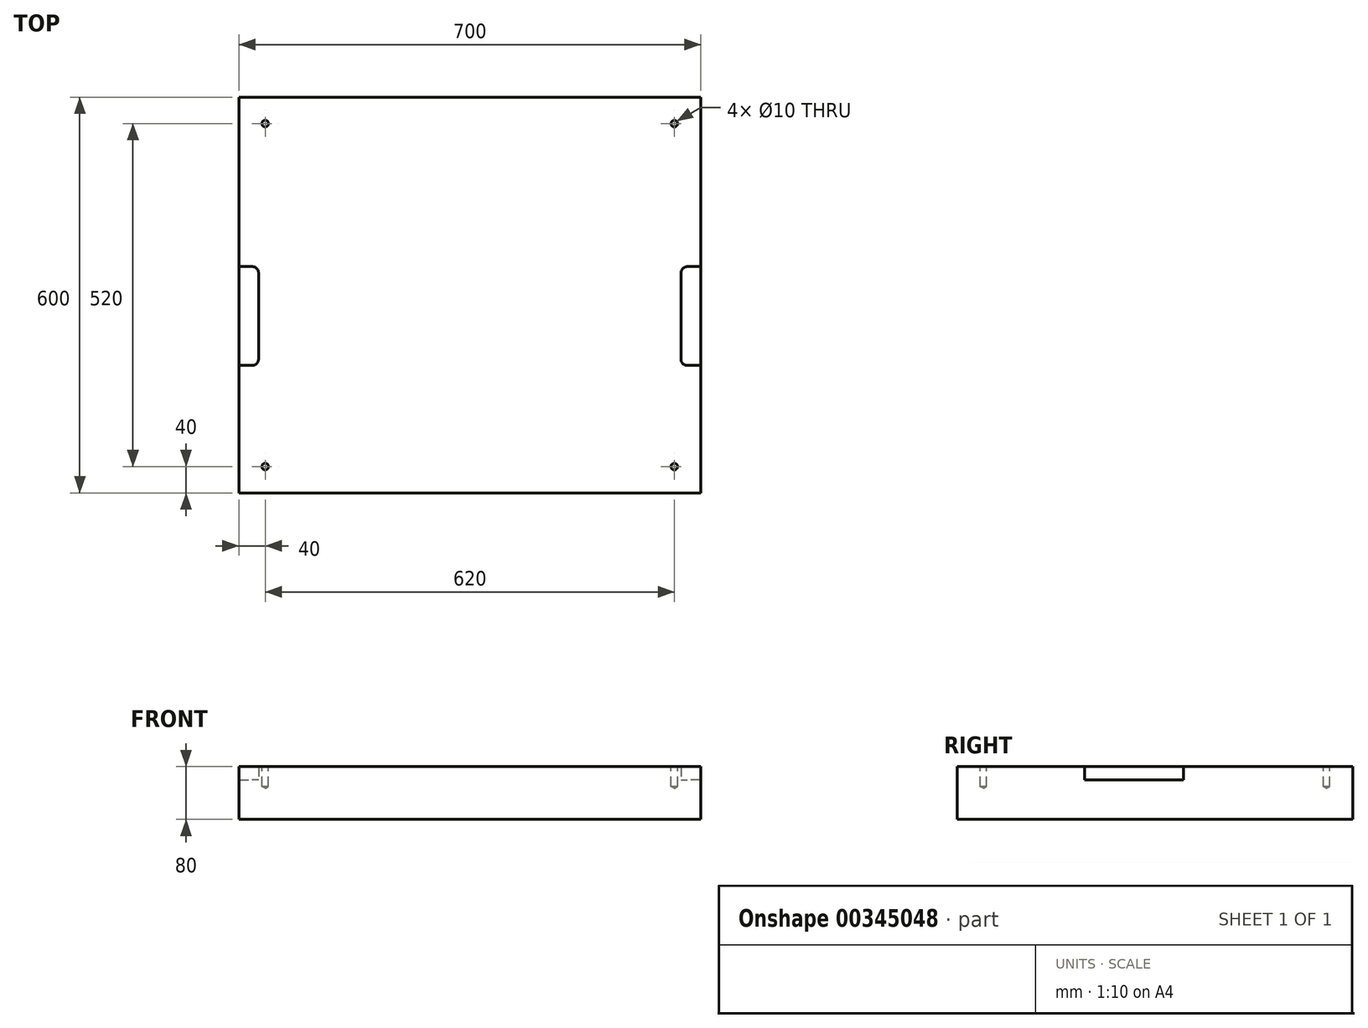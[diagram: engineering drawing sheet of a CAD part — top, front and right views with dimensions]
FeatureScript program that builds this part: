
annotation { "Feature Type Name" : "Feature", "Feature Type Description" : "" }
export const myFeature = defineFeature(function(context is Context, id is Id, definition is map)
    precondition{}
    {
        {
            var Q0;
            Q0=qCreatedBy(makeId("Top.planeOp"),FACE);
            var sketch = newSketch(context, id + "F0", { "sketchPlane" : qUnion([Q0])});
            skLineSegment(sketch, "E0.bottom", {"start": v(350, 300) * mm, "end": v(-350, 300) * mm});
            skLineSegment(sketch, "E0.top", {"start": v(350, -300) * mm, "end": v(-350, -300) * mm});
            skLineSegment(sketch, "E0.left", {"start": v(350, 300) * mm, "end": v(350, -300) * mm});
            skLineSegment(sketch, "E0.right", {"start": v(-350, 300) * mm, "end": v(-350, -300) * mm});
            skPoint(sketch, "E0.middle", {"position": v(0, 0) * mm});
            skLineSegment(sketch, "E1", {"start": v(-350, 0) * mm, "end": v(350, 0) * mm, "construction": true});
            skPoint(sketch, "E2.orphan", {"position": v(-210.42, 0) * mm});
            skLineSegment(sketch, "E3.bottom", {"start": v(350, 43.26) * mm, "end": v(330, 43.26) * mm});
            skLineSegment(sketch, "E3.top", {"start": v(350, -106.74) * mm, "end": v(330, -106.74) * mm});
            skLineSegment(sketch, "E3.left", {"start": v(350, 43.26) * mm, "end": v(350, -106.74) * mm});
            skLineSegment(sketch, "E3.right", {"start": v(320, 33.26) * mm, "end": v(320, -96.74) * mm});
            skPoint(sketch, "E4.visualSharp", {"position": v(320, -106.74) * mm});
            skArc(sketch, "E4.filletArc", {"start": v(320, -96.74) * mm, "mid": v(322.93, -103.8) * mm, "end": v(330, -106.74) * mm});
            skPoint(sketch, "E5.visualSharp", {"position": v(320, 43.26) * mm});
            skArc(sketch, "E5.filletArc", {"start": v(330, 43.26) * mm, "mid": v(322.93, 40.33) * mm, "end": v(320, 33.26) * mm});
            skLineSegment(sketch, "E6", {"start": v(0, 300) * mm, "end": v(0, -300) * mm, "construction": true});
            skLineSegment(sketch, "E7.MirrorCS", {"start": v(-350, 43.26) * mm, "end": v(-330, 43.26) * mm});
            skLineSegment(sketch, "E8.MirrorCS", {"start": v(-320, 33.26) * mm, "end": v(-320, -96.74) * mm});
            skArc(sketch, "E9.MirrorCS", {"start": v(-320, -96.74) * mm, "mid": v(-322.93, -103.8) * mm, "end": v(-330, -106.74) * mm});
            skArc(sketch, "E10.MirrorCS", {"start": v(-330, 43.26) * mm, "mid": v(-322.93, 40.33) * mm, "end": v(-320, 33.26) * mm});
            skLineSegment(sketch, "E11.MirrorCS", {"start": v(-350, -106.74) * mm, "end": v(-330, -106.74) * mm});
            skPoint(sketch, "E12", {"position": v(-310, 260) * mm});
            skPoint(sketch, "E13", {"position": v(310, 260) * mm});
            skPoint(sketch, "E14", {"position": v(310, -260) * mm});
            skPoint(sketch, "E15", {"position": v(-310, -260) * mm});
            skSolve(sketch);
        }
        {
            var Q0;
            Q0=makeQuery(id+"F0.imprint","IMPRINT",FACE,{"disambiguationData":[TD([[makeQuery(id+"F0.imprint","IMPRINT",EDGE,{"derivedFrom":sQuery(id+"F0.wireOp",EDGE,"E0.bottom")}),1.0]])]});
            extrude(context, id + "F1", {"entities" : qUnion([Q0]), "depth" : 80 * mm});
        }
        {
            var Q0;
            Q0=makeQuery(id+"F0.imprint","IMPRINT",FACE,{"disambiguationData":[TD([[makeQuery(id+"F0.imprint","IMPRINT",EDGE,{"derivedFrom":sQuery(id+"F0.wireOp",EDGE,"E3.bottom")}),1.0]])]});
            var Q1;
            {var subQ0=sQuery(id+"F0.wireOp",EDGE,"E7.MirrorCS");Q1=makeQuery(id+"F0.imprint","IMPRINT",FACE,{"disambiguationData":[TD([[makeQuery(id+"F0.imprint","IMPRINT",EDGE,{"derivedFrom":subQ0}),-1.0]])]});}
            extrude(context, id + "F2", {"entities" : qUnion([Q0, Q1]), "operationType" : NewBodyOperationType.ADD, "depth" : 60 * mm});
        }
        {
            var Q0;
            Q0=makeQuery(id+"F1.opExtrude","CAP_FACE",FACE,{"disambiguationData":[OSD([sQuery(id+"F0.wireOp",EDGE,"E0.bottom"),sQuery(id+"F0.wireOp",EDGE,"E0.top"),sQuery(id+"F0.wireOp",EDGE,"E0.left"),sQuery(id+"F0.wireOp",EDGE,"E0.right"),sQuery(id+"F0.wireOp",EDGE,"E3.bottom"),sQuery(id+"F0.wireOp",EDGE,"E3.top"),sQuery(id+"F0.wireOp",EDGE,"E3.right"),sQuery(id+"F0.wireOp",EDGE,"E4.filletArc"),sQuery(id+"F0.wireOp",EDGE,"E5.filletArc"),sQuery(id+"F0.wireOp",EDGE,"E7.MirrorCS"),sQuery(id+"F0.wireOp",EDGE,"E8.MirrorCS"),sQuery(id+"F0.wireOp",EDGE,"E9.MirrorCS"),sQuery(id+"F0.wireOp",EDGE,"E10.MirrorCS"),sQuery(id+"F0.wireOp",EDGE,"E11.MirrorCS")])],"isStart":false});
            var sketch = newSketch(context, id + "F3", { "sketchPlane" : qUnion([Q0])});
            skLineSegment(sketch, "E16.0", {"start": v(310, -260) * mm, "end": v(-310, -260) * mm, "construction": true});
            skLineSegment(sketch, "E16.1", {"start": v(310, 260) * mm, "end": v(310, -260) * mm, "construction": true});
            skLineSegment(sketch, "E16.2", {"start": v(310, 260) * mm, "end": v(-310, 260) * mm, "construction": true});
            skLineSegment(sketch, "E16.3", {"start": v(-310, 260) * mm, "end": v(-310, -260) * mm, "construction": true});
            skSolve(sketch);
        }
        {
            var Q0;
            Q0=sQuery(id+"F3.wireOp",VERTEX,"E16.1.end");
            var Q1;
            Q1=sQuery(id+"F3.wireOp",VERTEX,"E16.3.end");
            var Q2;
            Q2=sQuery(id+"F3.wireOp",VERTEX,"E16.2.start");
            var Q3;
            Q3=sQuery(id+"F3.wireOp",VERTEX,"E16.3.start");
            var Q4;
            Q4=makeQuery(id+"F1.opExtrude","SWEPT_BODY",BODY,{"disambiguationData":[OSD([sQuery(id+"F0.wireOp",EDGE,"E0.bottom"),sQuery(id+"F0.wireOp",EDGE,"E0.top"),sQuery(id+"F0.wireOp",EDGE,"E0.left"),sQuery(id+"F0.wireOp",EDGE,"E0.right"),sQuery(id+"F0.wireOp",EDGE,"E3.bottom"),sQuery(id+"F0.wireOp",EDGE,"E3.top"),sQuery(id+"F0.wireOp",EDGE,"E3.right"),sQuery(id+"F0.wireOp",EDGE,"E4.filletArc"),sQuery(id+"F0.wireOp",EDGE,"E5.filletArc"),sQuery(id+"F0.wireOp",EDGE,"E7.MirrorCS"),sQuery(id+"F0.wireOp",EDGE,"E8.MirrorCS"),sQuery(id+"F0.wireOp",EDGE,"E9.MirrorCS"),sQuery(id+"F0.wireOp",EDGE,"E10.MirrorCS"),sQuery(id+"F0.wireOp",EDGE,"E11.MirrorCS")])]});
            hole(context, id + "F4", {"style" : HoleStyle.SIMPLE, "endStyle" : HoleEndStyle.BLIND, "holeDiameter" : 10 * mm, "holeDepth" : 30 * mm, "isTappedThrough" : true, "tappedDepth" : 12 * mm, "tapClearance" : 3, "startFromSketch" : true, "locations" : qUnion([Q0, Q1, Q2, Q3]), "scope" : qUnion([Q4])});
        }
    });
